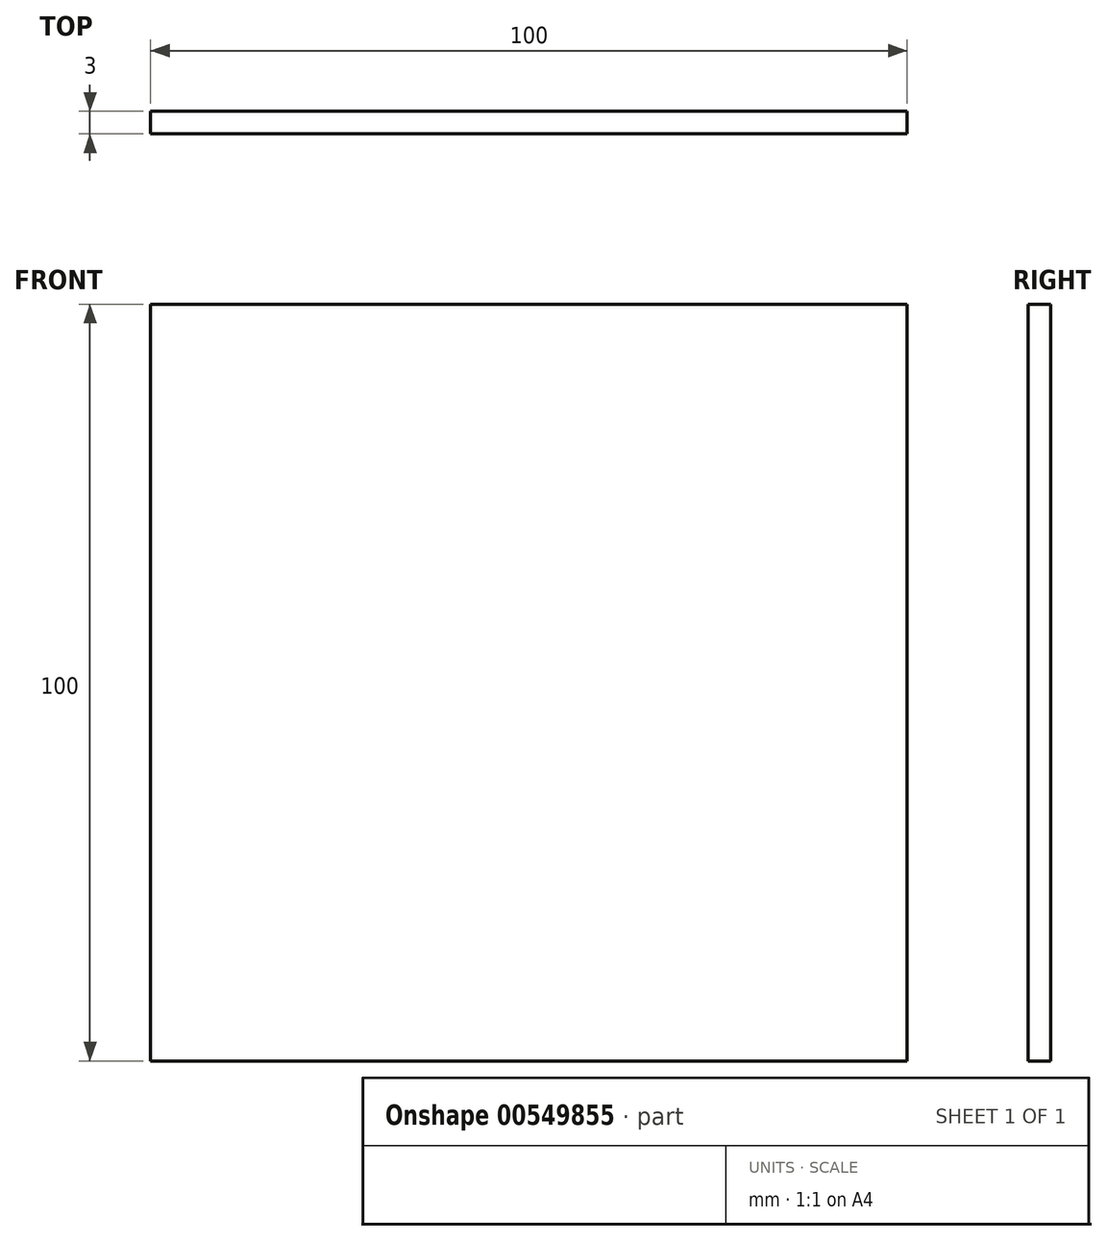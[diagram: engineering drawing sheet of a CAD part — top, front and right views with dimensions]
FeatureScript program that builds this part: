
annotation { "Feature Type Name" : "Feature", "Feature Type Description" : "" }
export const myFeature = defineFeature(function(context is Context, id is Id, definition is map)
    precondition{}
    {
        {
            var Q0;
            Q0=qCreatedBy(makeId("Front.planeOp"),FACE);
            var sketch = newSketch(context, id + "F0", { "sketchPlane" : qUnion([Q0])});
            skLineSegment(sketch, "E0.bottom", {"start": v(0, 0) * mm, "end": v(100, 0) * mm});
            skLineSegment(sketch, "E0.top", {"start": v(0, 100) * mm, "end": v(100, 100) * mm});
            skLineSegment(sketch, "E0.left", {"start": v(0, 0) * mm, "end": v(0, 100) * mm});
            skLineSegment(sketch, "E0.right", {"start": v(100, 0) * mm, "end": v(100, 100) * mm});
            skSolve(sketch);
        }
        {
            var Q0;
            Q0=makeQuery(id+"F0.imprint","IMPRINT",FACE,{"disambiguationData":[TD([[makeQuery(id+"F0.imprint","IMPRINT",EDGE,{"derivedFrom":sQuery(id+"F0.wireOp",EDGE,"E0.bottom")}),1.0]])]});
            extrude(context, id + "F1", {"entities" : qUnion([Q0]), "depth" : 3 * mm, "offsetDistance" : 25 * mm});
        }
    });
